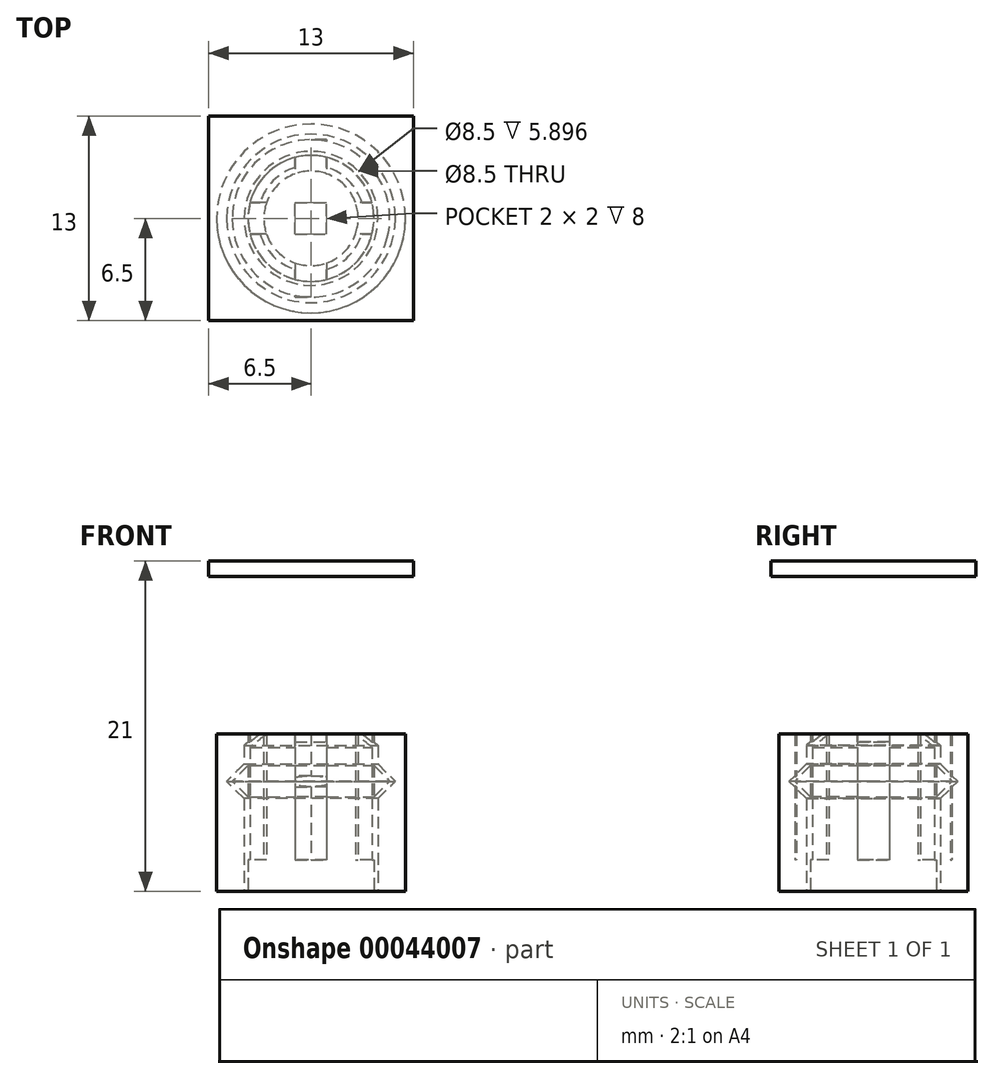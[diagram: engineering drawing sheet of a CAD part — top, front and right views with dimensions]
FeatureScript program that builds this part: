
annotation { "Feature Type Name" : "Feature", "Feature Type Description" : "" }
export const myFeature = defineFeature(function(context is Context, id is Id, definition is map)
    precondition{}
    {
        {
            var Q0;
            Q0=qCreatedBy(makeId("Front.planeOp"),FACE);
            var sketch = newSketch(context, id + "F0", { "sketchPlane" : qUnion([Q0])});
            skLineSegment(sketch, "E0", {"start": v(0, 10) * mm, "end": v(3, 10) * mm});
            skLineSegment(sketch, "E1", {"start": v(4, 9.16) * mm, "end": v(4, 8) * mm});
            skLineSegment(sketch, "E2", {"start": v(4, 8) * mm, "end": v(5, 7) * mm});
            skLineSegment(sketch, "E3", {"start": v(5, 7) * mm, "end": v(4, 6) * mm});
            skLineSegment(sketch, "E4", {"start": v(4, 6) * mm, "end": v(4, 0) * mm});
            skLineSegment(sketch, "E5", {"start": v(4, 0) * mm, "end": v(0, 0) * mm});
            skLineSegment(sketch, "E6", {"start": v(0, 0) * mm, "end": v(0, 10) * mm});
            skLineSegment(sketch, "E7", {"start": v(3, 10) * mm, "end": v(4, 9.16) * mm});
            skLineSegment(sketch, "E8", {"start": v(5, 7) * mm, "end": v(0, 7) * mm, "construction": true});
            skSolve(sketch);
        }
        {
            var Q0;
            Q0=makeQuery(id+"F0.imprint","IMPRINT",FACE,{"disambiguationData":[TD([[makeQuery(id+"F0.imprint","IMPRINT",EDGE,{"derivedFrom":sQuery(id+"F0.wireOp",EDGE,"E0")}),-1.0]])]});
            var Q1;
            Q1=sQuery(id+"F0.wireOp",EDGE,"E6");
            revolve(context, id + "F1", {"entities" : qUnion([Q0]), "axis" : qUnion([Q1]), "revolveType" : RevolveType.FULL});
        }
        {
            var Q0;
            Q0=qCreatedBy(makeId("Top.planeOp"),FACE);
            var sketch = newSketch(context, id + "F2", { "sketchPlane" : qUnion([Q0])});
            skCircle(sketch, "E9.0", {"center": v(0, 0) * mm, "radius": 5 * mm});
            skCircle(sketch, "E10.0", {"center": v(0, 0) * mm, "radius": 4 * mm});
            skCircle(sketch, "E11.0", {"center": v(0, 0) * mm, "radius": 3 * mm});
            skLineSegment(sketch, "E12.rect.bottom", {"start": v(-1, 5) * mm, "end": v(1, 5) * mm});
            skLineSegment(sketch, "E12.rect.top", {"start": v(-1, -5) * mm, "end": v(1, -5) * mm});
            skLineSegment(sketch, "E12.rect.left", {"start": v(-1, 5) * mm, "end": v(-1, -5) * mm});
            skLineSegment(sketch, "E12.rect.right", {"start": v(1, 5) * mm, "end": v(1, -5) * mm});
            skPoint(sketch, "E13", {"position": v(0, 5) * mm});
            skPoint(sketch, "E14", {"position": v(0, -5) * mm});
            skLineSegment(sketch, "E15.1.0", {"start": v(5, 1) * mm, "end": v(-5, 1) * mm});
            skLineSegment(sketch, "E15.1.1", {"start": v(5, -1) * mm, "end": v(-5, -1) * mm});
            skLineSegment(sketch, "E15.1.2", {"start": v(5, 1) * mm, "end": v(5, -1) * mm});
            skLineSegment(sketch, "E15.1.3", {"start": v(-5, 1) * mm, "end": v(-5, -1) * mm});
            skLineSegment(sketch, "E15.anchor1", {"start": v(0, 0) * mm, "end": v(1, -5) * mm, "construction": true});
            skLineSegment(sketch, "E15.anchor2", {"start": v(0, 0) * mm, "end": v(-5, -1) * mm, "construction": true});
            skSolve(sketch);
        }
        {
            var Q0;
            Q0=qCreatedBy(makeId("Top.planeOp"),FACE);
            var sketch = newSketch(context, id + "F3", { "sketchPlane" : qUnion([Q0])});
            skCircle(sketch, "E16", {"center": v(0, 0) * mm, "radius": 6 * mm});
            skSolve(sketch);
        }
        {
            var Q0;
            Q0 = qSketchRegion(id + "F3", true);
            var Q1;
            {var subQ1=sQuery(id+"F2.wireOp",EDGE,"E12.rect.left");var subQ3=sQuery(id+"F2.wireOp",EDGE,"E11.0");var subQ5=sQuery(id+"F2.wireOp",EDGE,"E10.0");var subQ7=sQuery(id+"F2.wireOp",EDGE,"E9.0");var subQ8=makeQuery(id+"F2.imprint","INTERSECT",VERTEX,{"disambiguationData":[OD(0.0)],"derivedFrom":[subQ3,subQ1]});var subQ9=makeQuery(id+"F2.imprint","INTERSECT",VERTEX,{"disambiguationData":[OD(1.0)],"derivedFrom":[subQ5,subQ1]});Q1=makeQuery(id+"F6.boolean.opBoolean","SPLIT",FACE,{"disambiguationData":[TD([makeQuery(id+"F6.opExtrude","SWEPT_FACE",FACE,{"disambiguationData":[OSD([subQ1]),TDD([makeQuery(id+"F2.imprint","IMPRINT",EDGE,{"disambiguationData":[TD([[subQ8,1.0]])],"derivedFrom":subQ1}),makeQuery(id+"F2.imprint","IMPRINT",EDGE,{"disambiguationData":[TD([[subQ9,1.0]])],"derivedFrom":subQ1}),makeQuery(id+"F2.imprint","IMPRINT",EDGE,{"disambiguationData":[TD([[makeQuery(id+"F2.imprint","INTERSECT",VERTEX,{"disambiguationData":[OD(0.0)],"derivedFrom":[subQ7,subQ1]}),1.0]])],"derivedFrom":subQ1})])]})])],"derivedFrom":makeQuery(id+"F1.opRevolve","SWEPT_FACE",FACE,{"disambiguationData":[OSD([sQuery(id+"F0.wireOp",EDGE,"E0")])]})});}
            extrude(context, id + "F4", {"entities" : qUnion([Q0]), "endBound" : BoundingType.UP_TO_SURFACE, "endBoundEntityFace" : qUnion([Q1]), "depth" : 25 * mm});
        }
        {
            var Q0;
            Q0=makeQuery(id+"F1.opRevolve","SWEPT_BODY",BODY,{"disambiguationData":[OSD([sQuery(id+"F0.wireOp",EDGE,"E0"),sQuery(id+"F0.wireOp",EDGE,"E1"),sQuery(id+"F0.wireOp",EDGE,"E2"),sQuery(id+"F0.wireOp",EDGE,"E3"),sQuery(id+"F0.wireOp",EDGE,"E4"),sQuery(id+"F0.wireOp",EDGE,"E5"),sQuery(id+"F0.wireOp",EDGE,"E6"),sQuery(id+"F0.wireOp",EDGE,"E7")])]});
            var Q1;
            Q1=makeQuery(id+"F4.opExtrude","SWEPT_BODY",BODY,{"disambiguationData":[OSD([sQuery(id+"F3.wireOp",EDGE,"E16")])]});
            booleanBodies(context, id + "F5", {"operationType" : BooleanOperationType.SUBTRACTION, "tools" : qUnion([Q0]), "targets" : qUnion([Q1]), "offset" : true, "offsetAll" : true, "offsetDistance" : 0.25 * mm, "keepTools" : true});
        }
        {
            var Q0;
            {var subQ0=sQuery(id+"F2.wireOp",EDGE,"E12.rect.right");var subQ3=sQuery(id+"F2.wireOp",EDGE,"E9.0");var subQ4=makeQuery(id+"F2.imprint","INTERSECT",VERTEX,{"disambiguationData":[OD(0.0)],"derivedFrom":[subQ3,subQ0]});Q0=makeQuery(id+"F2.imprint","IMPRINT",FACE,{"disambiguationData":[TD([[makeQuery(id+"F2.imprint","IMPRINT",EDGE,{"disambiguationData":[TD([[subQ4,-1.0]])],"derivedFrom":subQ3}),-1.0]])]});}
            var Q1;
            {var subQ0=sQuery(id+"F2.wireOp",EDGE,"E15.1.1");var subQ3=sQuery(id+"F2.wireOp",EDGE,"E9.0");var subQ4=makeQuery(id+"F2.imprint","INTERSECT",VERTEX,{"disambiguationData":[OD(0.0)],"derivedFrom":[subQ3,subQ0]});Q1=makeQuery(id+"F2.imprint","IMPRINT",FACE,{"disambiguationData":[TD([[makeQuery(id+"F2.imprint","IMPRINT",EDGE,{"disambiguationData":[TD([[subQ4,1.0]])],"derivedFrom":subQ3}),-1.0]])]});}
            var Q2;
            {var subQ0=sQuery(id+"F2.wireOp",EDGE,"E15.1.1");var subQ3=sQuery(id+"F2.wireOp",EDGE,"E9.0");var subQ4=makeQuery(id+"F2.imprint","INTERSECT",VERTEX,{"disambiguationData":[OD(1.0)],"derivedFrom":[subQ3,subQ0]});Q2=makeQuery(id+"F2.imprint","IMPRINT",FACE,{"disambiguationData":[TD([[makeQuery(id+"F2.imprint","IMPRINT",EDGE,{"disambiguationData":[TD([[subQ4,-1.0]])],"derivedFrom":subQ3}),-1.0]])]});}
            var Q3;
            {var subQ3=sQuery(id+"F2.wireOp",EDGE,"E10.0");var subQ5=sQuery(id+"F2.wireOp",EDGE,"E12.rect.left");var subQ7=makeQuery(id+"F2.imprint","INTERSECT",VERTEX,{"disambiguationData":[OD(1.0)],"derivedFrom":[subQ3,subQ5]});Q3=makeQuery(id+"F2.imprint","IMPRINT",FACE,{"disambiguationData":[TD([[makeQuery(id+"F2.imprint","IMPRINT",EDGE,{"disambiguationData":[TD([[subQ7,-1.0]])],"derivedFrom":subQ3}),1.0]])]});}
            var Q4;
            {var subQ3=sQuery(id+"F2.wireOp",EDGE,"E11.0");var subQ5=sQuery(id+"F2.wireOp",EDGE,"E12.rect.right");var subQ7=makeQuery(id+"F2.imprint","INTERSECT",VERTEX,{"disambiguationData":[OD(0.0)],"derivedFrom":[subQ3,subQ5]});Q4=makeQuery(id+"F2.imprint","IMPRINT",FACE,{"disambiguationData":[TD([[makeQuery(id+"F2.imprint","IMPRINT",EDGE,{"disambiguationData":[TD([[subQ7,-1.0]])],"derivedFrom":subQ3}),-1.0]])]});}
            var Q5;
            {var subQ3=sQuery(id+"F2.wireOp",EDGE,"E12.rect.left");var subQ5=sQuery(id+"F2.wireOp",EDGE,"E15.1.0");var subQ7=makeQuery(id+"F2.imprint","INTERSECT",VERTEX,{"derivedFrom":[subQ3,subQ5]});Q5=makeQuery(id+"F2.imprint","IMPRINT",FACE,{"disambiguationData":[TD([[makeQuery(id+"F2.imprint","IMPRINT",EDGE,{"disambiguationData":[TD([[subQ7,-1.0]])],"derivedFrom":subQ3}),1.0]])]});}
            var Q6;
            {var subQ0=sQuery(id+"F2.wireOp",EDGE,"E15.1.1");var subQ3=sQuery(id+"F2.wireOp",EDGE,"E11.0");var subQ4=makeQuery(id+"F2.imprint","INTERSECT",VERTEX,{"disambiguationData":[OD(1.0)],"derivedFrom":[subQ3,subQ0]});Q6=makeQuery(id+"F2.imprint","IMPRINT",FACE,{"disambiguationData":[TD([[makeQuery(id+"F2.imprint","IMPRINT",EDGE,{"disambiguationData":[TD([[subQ4,-1.0]])],"derivedFrom":subQ3}),-1.0]])]});}
            var Q7;
            {var subQ0=sQuery(id+"F2.wireOp",EDGE,"E15.1.0");var subQ3=sQuery(id+"F2.wireOp",EDGE,"E10.0");var subQ4=makeQuery(id+"F2.imprint","INTERSECT",VERTEX,{"disambiguationData":[OD(1.0)],"derivedFrom":[subQ3,subQ0]});Q7=makeQuery(id+"F2.imprint","IMPRINT",FACE,{"disambiguationData":[TD([[makeQuery(id+"F2.imprint","IMPRINT",EDGE,{"disambiguationData":[TD([[subQ4,-1.0]])],"derivedFrom":subQ3}),1.0]])]});}
            var Q8;
            {var subQ3=sQuery(id+"F2.wireOp",EDGE,"E11.0");var subQ5=sQuery(id+"F2.wireOp",EDGE,"E15.1.1");var subQ7=makeQuery(id+"F2.imprint","INTERSECT",VERTEX,{"disambiguationData":[OD(0.0)],"derivedFrom":[subQ3,subQ5]});Q8=makeQuery(id+"F2.imprint","IMPRINT",FACE,{"disambiguationData":[TD([[makeQuery(id+"F2.imprint","IMPRINT",EDGE,{"disambiguationData":[TD([[subQ7,1.0]])],"derivedFrom":subQ3}),-1.0]])]});}
            var Q9;
            {var subQ0=sQuery(id+"F2.wireOp",EDGE,"E15.1.0");var subQ3=sQuery(id+"F2.wireOp",EDGE,"E10.0");var subQ4=makeQuery(id+"F2.imprint","INTERSECT",VERTEX,{"disambiguationData":[OD(0.0)],"derivedFrom":[subQ3,subQ0]});Q9=makeQuery(id+"F2.imprint","IMPRINT",FACE,{"disambiguationData":[TD([[makeQuery(id+"F2.imprint","IMPRINT",EDGE,{"disambiguationData":[TD([[subQ4,1.0]])],"derivedFrom":subQ3}),1.0]])]});}
            var Q10;
            {var subQ3=sQuery(id+"F2.wireOp",EDGE,"E11.0");var subQ5=sQuery(id+"F2.wireOp",EDGE,"E12.rect.left");var subQ7=makeQuery(id+"F2.imprint","INTERSECT",VERTEX,{"disambiguationData":[OD(1.0)],"derivedFrom":[subQ3,subQ5]});Q10=makeQuery(id+"F2.imprint","IMPRINT",FACE,{"disambiguationData":[TD([[makeQuery(id+"F2.imprint","IMPRINT",EDGE,{"disambiguationData":[TD([[subQ7,-1.0]])],"derivedFrom":subQ3}),-1.0]])]});}
            var Q11;
            {var subQ1=sQuery(id+"F2.wireOp",EDGE,"E12.rect.right");var subQ5=sQuery(id+"F2.wireOp",EDGE,"E10.0");var subQ6=makeQuery(id+"F2.imprint","INTERSECT",VERTEX,{"disambiguationData":[OD(0.0)],"derivedFrom":[subQ5,subQ1]});Q11=makeQuery(id+"F2.imprint","IMPRINT",FACE,{"disambiguationData":[TD([[makeQuery(id+"F2.imprint","IMPRINT",EDGE,{"disambiguationData":[TD([[subQ6,-1.0]])],"derivedFrom":subQ5}),1.0]])]});}
            var Q12;
            {var subQ0=sQuery(id+"F2.wireOp",EDGE,"E9.0");var subQ2=sQuery(id+"F2.wireOp",EDGE,"E12.rect.left");var subQ3=makeQuery(id+"F2.imprint","INTERSECT",VERTEX,{"disambiguationData":[OD(1.0)],"derivedFrom":[subQ0,subQ2]});Q12=makeQuery(id+"F2.imprint","IMPRINT",FACE,{"disambiguationData":[TD([[makeQuery(id+"F2.imprint","IMPRINT",EDGE,{"disambiguationData":[TD([[subQ3,-1.0]])],"derivedFrom":subQ0}),-1.0]])]});}
            var Q13;
            Q13=makeQuery(id+"F1.opRevolve","SWEPT_FACE",FACE,{"disambiguationData":[OSD([sQuery(id+"F0.wireOp",EDGE,"E0")])]});
            extrude(context, id + "F6", {"entities" : qUnion([Q0, Q1, Q2, Q3, Q4, Q5, Q6, Q7, Q8, Q9, Q10, Q11, Q12]), "operationType" : NewBodyOperationType.REMOVE, "endBound" : BoundingType.UP_TO_SURFACE, "endBoundEntityFace" : qUnion([Q13]), "depth" : 25 * mm, "hasSecondDirection" : true, "secondDirectionOppositeDirection" : false, "secondDirectionDepth" : 2 * mm});
        }
        {
            var Q0;
            Q0=qCreatedBy(makeId("Top.planeOp"),FACE);
            cPlane(context, id + "F7", {"entities" : qUnion([Q0]), "cplaneType" : CPlaneType.OFFSET, "offset" : 20 * mm, "width" : 150 * mm, "height" : 150 * mm});
        }
        {
            var Q0;
            Q0=qCreatedBy(id+"F7.planeOp",FACE);
            var sketch = newSketch(context, id + "F8", { "sketchPlane" : qUnion([Q0])});
            skLineSegment(sketch, "E17.rect.bottom", {"start": v(-6.5, 6.5) * mm, "end": v(6.5, 6.5) * mm});
            skLineSegment(sketch, "E17.rect.top", {"start": v(-6.5, -6.5) * mm, "end": v(6.5, -6.5) * mm});
            skLineSegment(sketch, "E17.rect.left", {"start": v(-6.5, 6.5) * mm, "end": v(-6.5, -6.5) * mm});
            skLineSegment(sketch, "E17.rect.right", {"start": v(6.5, 6.5) * mm, "end": v(6.5, -6.5) * mm});
            skPoint(sketch, "E17.rect.middle", {"position": v(0, 0) * mm});
            skSolve(sketch);
        }
        {
            var Q0;
            Q0=makeQuery(id+"F8.imprint","IMPRINT",FACE,{"disambiguationData":[TD([[makeQuery(id+"F8.imprint","IMPRINT",EDGE,{"derivedFrom":sQuery(id+"F8.wireOp",EDGE,"E17.rect.bottom")}),-1.0]])]});
            extrude(context, id + "F9", {"entities" : qUnion([Q0]), "depth" : 1 * mm});
        }
    });
